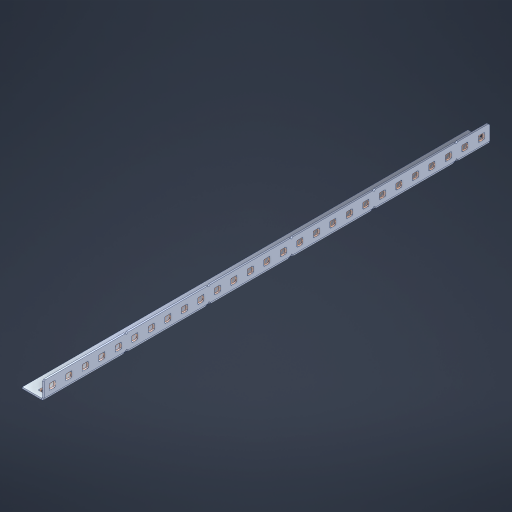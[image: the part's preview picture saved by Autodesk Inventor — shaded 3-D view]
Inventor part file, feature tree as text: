
AUTODESK INVENTOR PART (.ipt)
format: ipt  version: 2023 (Build 270158000, 158)  size: 894,464 bytes
history: native  units: in
note: dims shown in document units (in); Inventor stores cm internally (conversion verified against a paired STEP export)
features: other x59, extrude x53, sheet_metal_op x10, sketch x8, mirror x1, pattern_linear x1, chamfer x1
ambient origin geometry x8: Origin, YZ Plane, XZ Plane, XY Plane, X Axis, Y Axis, Z Axis, Center Point
bodies: Solid1 (feature_tree), Body (feature_tree)
feature tree (133):
  other  "Flange Pattern Plane"
  sheet_metal_op  "Flange Pattern"
  sheet_metal_op  "Body Pattern"
  other  "Arc Length"
  mirror  "Notch Mirror"
  pattern_linear  "Notch Pattern"  Spacing1=0.1875in  [1 undecoded]
  chamfer  "End Chamfer"
  extrude  "Half Cut"  Depth=0.0469in
  sketch  "Sketch1"  dims[d0=2.5in]
  other  "Plate1"
  sketch  "Sketch2"  dims[d1=13.5in]
  other  "Plate2"
  sheet_metal_op  "Bend1"
  sheet_metal_op  "Corner1"
  sketch  "Sketch3"  dims[d2=0.0469in]
  other  "Flange Pattern Sketch"
  sketch  "Sketch7"  dims[d3=0.0469in]
  other  "Srf1"
  other  "Srf2"
  sketch  "Sketch8"  dims[d4=0.0234in]
  sketch  "Sketch9"  dims[d5=0.0938in]
  other  "Srf91"
  sheet_metal_op  "Body Pattern Sketch"
  other  "Srf92"
  sketch  "Sketch13"  dims[d6=0.0469in]
  sketch  "Sketch14"  dims[d7=0.5in d8=90.0deg d9=0.0312in d10=0.1875in d11=0.0469in d12=0.0469in d16=0.182in d17=0.02in d18=0.0469in d19=0.0in d20=0.25in d21=0.25in d46=0.172in d47=1.0in d48=0.0in d49=0.182in d50=0.02in d51=0.25in d52=0.25in d53=0.0469in d54=0.0in d55=0.172in d56=1.0in d57=0.0in d60=10.6299in d62=0.5in d63=0.3937in d65=0.5in d85=0.1227in d86=0.1659in d88=0.04in d89=0.0469in d90=0.0in d91=0.04in d92=0.0491in d95=2.5in d96=0.04in d97=0.25in d98=45.0deg d101=0.0in d102=2.497in d131=0.5in d132=10.6299in d134=0.5in d139=0.5in]
  other  "Srf856"
  other  "Srf1310"
  other  "Srf1311"
  other  "Srf1312"
  other  "Srf1376"
  other  "Srf1377"
  other  "Srf1728"
  other  "Srf1755"
  other  "Srf1878"
  other  "Srf1879"
  other  "Srf1880"
  other  "Srf1881"
  other  "Srf1882"
  other  "Srf1883"
  other  "Srf1884"
  other  "Srf1885"
  other  "Srf1886"
  other  "Srf1887"
  other  "Srf1888"
  other  "Srf1889"
  other  "Srf1890"
  other  "Srf1891"
  other  "Srf1892"
  other  "Srf1893"
  other  "Srf1894"
  other  "Srf1895"
  other  "Srf1896"
  other  "Srf1897"
  other  "Srf1898"
  other  "Srf1942"
  other  "Srf1943"
  other  "Srf1944"
  other  "Srf1945"
  other  "Srf1946"
  other  "Srf1947"
  other  "Srf1948"
  other  "Srf1949"
  other  "Srf1950"
  other  "Srf1951"
  other  "Srf1952"
  other  "Srf1953"
  other  "Srf1954"
  other  "Srf1955"
  other  "Srf1956"
  other  "Srf1957"
  other  "Srf1958"
  other  "Srf1959"
  other  "Srf1960"
  other  "Srf1961"
  other  "Srf1962"
  sheet_metal_op  "Flange Stamp"
  sheet_metal_op  "Flange Circle"
  sheet_metal_op  "Body Stamp"
  sheet_metal_op  "Body Circle"
  sheet_metal_op  "Notch"
  extrude  "ExtrusionSrf2"  Depth=0.0469in
  extrude  "ExtrusionSrf92"  Depth=0.5in
  extrude  "ExtrusionSrf856"  Depth=0.02in
  extrude  "ExtrusionSrf1310"  Depth=0.0469in
  extrude  "ExtrusionSrf1311"  TaperAngle=0.0deg  [1 undecoded]
  extrude  "ExtrusionSrf1312"  Depth=0.5in
  extrude  "ExtrusionSrf1376"  Depth=0.5in
  extrude  "ExtrusionSrf1377"  Depth=0.5in
  extrude  "ExtrusionSrf1728"  Depth=0.5in TaperAngle=0.0deg
  extrude  "ExtrusionSrf1755"  Depth=0.5in
  extrude  "ExtrusionSrf1878"  Depth=0.02in
  extrude  "ExtrusionSrf1879"  Depth=0.5in
  extrude  "ExtrusionSrf1880"  Depth=0.5in
  extrude  "ExtrusionSrf1881"  Depth=0.0469in
  extrude  "ExtrusionSrf1882"  TaperAngle=0.0deg  [1 undecoded]
  extrude  "ExtrusionSrf1883"  Depth=0.5in
  extrude  "ExtrusionSrf1884"  Depth=0.5in TaperAngle=0.0deg
  extrude  "ExtrusionSrf1885"  Depth=0.5in
  extrude  "ExtrusionSrf1886"  Depth=0.5in
  extrude  "ExtrusionSrf1887"  Depth=0.5in
  extrude  "ExtrusionSrf1888"  Depth=0.5in
  extrude  "ExtrusionSrf1889"  Depth=0.5in
  extrude  "ExtrusionSrf1890"  Depth=0.0469in
  extrude  "ExtrusionSrf1891"  TaperAngle=0.0deg  [1 undecoded]
  extrude  "ExtrusionSrf1892"  Depth=0.5in
  extrude  "ExtrusionSrf1893"  Depth=0.5in
  extrude  "ExtrusionSrf1894"  Depth=0.5in
  extrude  "ExtrusionSrf1895"  Depth=0.5in TaperAngle=45.0deg
  extrude  "ExtrusionSrf1896"  TaperAngle=0.0deg  [1 undecoded]
  extrude  "ExtrusionSrf1897"  Depth=0.5in
  extrude  "ExtrusionSrf1898"  Depth=0.5in
  extrude  "ExtrusionSrf1942"  Depth=0.5in
  extrude  "ExtrusionSrf1943"  Depth=0.5in
  extrude  "ExtrusionSrf1944"  Depth=0.5in
  extrude  "ExtrusionSrf1945"  [1 undecoded]
  extrude  "ExtrusionSrf1946"  [1 undecoded]
  extrude  "ExtrusionSrf1947"  [1 undecoded]
  extrude  "ExtrusionSrf1948"  [1 undecoded]
  extrude  "ExtrusionSrf1949"  [1 undecoded]
  extrude  "ExtrusionSrf1950"  [1 undecoded]
  extrude  "ExtrusionSrf1951"  [1 undecoded]
  extrude  "ExtrusionSrf1952"  [1 undecoded]
  extrude  "ExtrusionSrf1953"  [1 undecoded]
  extrude  "ExtrusionSrf1954"  [1 undecoded]
  extrude  "ExtrusionSrf1955"  [1 undecoded]
  extrude  "ExtrusionSrf1956"  [1 undecoded]
  extrude  "ExtrusionSrf1957"  [1 undecoded]
  extrude  "ExtrusionSrf1958"  [1 undecoded]
  extrude  "ExtrusionSrf1959"  [1 undecoded]
  extrude  "ExtrusionSrf1960"  [1 undecoded]
  extrude  "ExtrusionSrf1961"  [1 undecoded]
  extrude  "ExtrusionSrf1962"  [1 undecoded]
note: 23 required parameter values undecoded (feature->parameter linkage not recoverable at this tier; creation-order binding heuristic only, values carry confidence <= 0.55)
